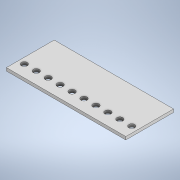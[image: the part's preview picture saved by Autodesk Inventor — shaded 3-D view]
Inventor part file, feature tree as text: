
AUTODESK INVENTOR PART (.ipt)
format: ipt  version: 2020.2 (Build 242310000, 310)  size: 124,928 bytes
history: native  units: in
note: dims shown in document units (in); Inventor stores cm internally (conversion verified against a paired STEP export)
features: extrude x2, sketch x2
ambient origin geometry x8: Origin, YZ Plane, XZ Plane, XY Plane, X Axis, Y Axis, Z Axis, Center Point
bodies: Solid1 (feature_tree)
feature tree (4):
  extrude  "Extrusion1"  Depth=0.25in
  extrude  "Extrusion2"  Depth=10.0in
  sketch  "Sketch1"  dims[d0=0.25in d1=0.0in d2=3.0in]
  sketch  "Sketch3"  dims[d3=4.0in d4=0.5in d5=0.5in d6=3.937in d8=1.0in d9=0.3937in d11=1.0in d13=10.0in d14=0.0in d15=0.0in]
